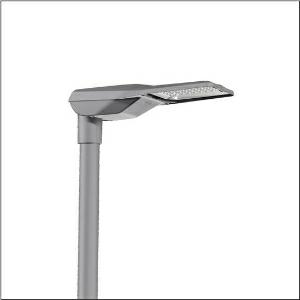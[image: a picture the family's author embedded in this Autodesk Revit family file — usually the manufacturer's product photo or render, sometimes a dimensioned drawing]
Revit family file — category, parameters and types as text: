
# Revit family: streetlight_sl_21_iq_mini___p1_0a_5xe2a31d08gb_969e
name_source: partatom
category: Lighting Fixtures
units: mm (PartAtom-declared; Revit-internal decimal feet)

## family parameters
Cut with Voids When Loaded = No
Host = Face
Light Source = No
Part Type = Normal
Room Calculation Point = No
Round Connector Dimension = Use Diameter
Shared = No

## types (1)
- --- (1 x LED, 5680 lm, 37.1 W, 3000K)
    Apparent Load = 37 VA
    CIE Flux Codes = 21 50 90 100 100
    Color Rendering = 70
    Color Temperature = 3000K
    Default Elevation = 1800 mm
    Description = Streetlight SL 21 mini, mast luminaire, primary light control with lens, of PMMA, primary optical cover: cover, of toughened safety glass, transparent, light distribution: P1.0a, light emission: direct distribution, primary light characteristic: asymmetric, installation type: post-top, side-entry, LED, High Power LED, rated luminous flux: 5.680lm, luminous efficacy: 153lm/W, light colour: 730, colour temperature: 3000K, control gear: ECG iQ, control: Auto-Match, Temp-Guard, Lumen-Switch, Night-Set, Smart-Wire, Light-Fading, Desk-Remote (wireless, voltage-free reading and setting of iQ features in the workshop via application-optimized NFC function/RFID function), optimised constant luminous flux control (CLO 2.0), mains connection: 220..240V, AC, 50/60Hz, start of lifetime: 37W, end of lifetime: 39W, reduction: 18W, luminaire housing, of diecast aluminium, powder-coated, Siteco® metallic grey (DB 702S), corrosivity category C5 according to DIN EN ISO 12944, length: 628mm, width: 235mm, height: 110mm, spigot size: 60/76mm (post-top) and 42/60/76mm (side-entry), mast flange for spigot size: 42mm: 5XC10008XM4, 60mm: 5XC10008XM2, 76/60mm: 5XC10108XM1, protection rating (complete): IP66, insulation class (complete): insulation class II (safety insulation), certification: CE, ENEC, VDE, impact resistance: IK09, permissible operating ambient temperature for outdoor applications: -40..+50°C, standard-compliant lighting for roads and squares, packaging unit: 1 piece

Light Distribution: P1.0a
    Height = 110 mm
    Lamp = 1 x LED
    Lamp Light Flux = 5680 lm
    Lamp Power = 37.1 W
    Lamp count = 1
    Length = 625 mm
    Luminous efficacy = 153 lm/W
    Manufacturer = Siteco
    ModVariant = No
    Model = 5XE2A31D08GB
    Number of Poles = 1
    OnlyDefault = Yes
    Power Factor = 1
    Product Name = Streetlight SL 21 iQ mini | P1.0a
    Product group = mast luminaire | pylon top
    ProductGroupID = 6100
    Protection Class = Protection class II
    Protection Degree = IP 66
    RLX_Detail_Level = 1
    RlxData = <blob elided: 103085 chars, md5=7c34e63c>
    Socket = socket
    Standby Power = 0 W
    System Light Flux = 5680 lm
    System Power = 37 W
    Type Comments = factory setting: luminous flux: 100 % | dim-lin: 254 | 385 mA
    Type Image = l_1003519.jpg
    URL = http://relux.com
    VarID = @adj_103925
    Voltage = 0 V
    Weight = 0.00 kg
    Width = 234 mm

## geometry (parser evidence)
native form markers: Blend x4, Sweep x11
no freeform markers — native parametric forms only
